# Revit family: Plumbing_Fixtures-Grohe-K7_Level_Sink_Mixer_Chrome-12-METRIC
name_source: partatom
category: Plumbing Fixtures
revit_build: Autodesk Revit Architecture 2012 (Build: 20110916_2132(x64)
units: mm (PartAtom-declared; Revit-internal decimal feet)

## types (1)
- K7_Sink_Mixer_32950000
    ADA Compliant = Yes
    Assembly Code = C1030220
    AssetType = Fixed
    Barcode = 0
    CW Connection = Yes
    CWFU = 4.5
    Cold Water Conection Diamiter = 10 mm  [stored 0.0328084 ft]
    Cold Water Radius = 5 mm  [stored 0.0164042 ft]
    Control Handle = Yes
    Control Handle Center = Yes
    Cost = 0 $
    Default Elevation = 600 mm
    Ecojoy = No
    ExpectedLife = 0
    Faucet Material = Grohe-Chrome
    Flow Rate = 9L/min
    HW Connection = Yes
    HWFU = 4.5
    Height = 674 mm
    Hot Water Conection Diamiter = 10 mm  [stored 0.0328084 ft]
    Hot Water Radius = 5 mm  [stored 0.0164042 ft]
    Keynote = N13
    Length = 234 mm
    Low Emitting Material = Yes
    Manufacturer = Grohe AG
    Mixing Leaver = Yes
    Model = K7 Sink Mixer
    ModelNumber = K7 Sink Mixer
    Name = K7 Sink Mixer
    No of Holes = 1
    Operating Pressure = 3 bar
    Percentage of Recycled Content = 0
    Product Documentation Link = http://cdn08.grohe.com
    Product Page URL = http://www.grohe.com
    Pull out or Pull Down = Pull Out
    SerialNumber = 0
    Spare Parts List = http://www.grohe.com
    TagNumber = 0
    URL = www.grohe.com
    Valve Spacing = 34 mm
    Vent Connection = No
    WFU = 0
    Waste Connection = No
    Width = 234 mm
    _BIMspec_GUID = 0
    _current revision = 1
    _distributed by = www.bimstore.co.uk

note: [stored X ft] marks values corroborated as IEEE doubles in the binary element streams (Revit-internal decimal feet)

## geometry (parser evidence)
native form markers: Blend x2, Sweep x2
no freeform markers — native parametric forms only
